# Revit family: BIMLIB_ДымовойСтеновойКлапан_SHSD_Прямоугольный_SHUFT
name_source: partatom
category: Арматура воздуховодов
revit_build: Autodesk Revit 2017 (Build: 20170118_1100(x64)
units: mm (PartAtom-declared; Revit-internal decimal feet)

## family parameters
Всегда вертикально = Да
На основе рабочей плоскости = Нет
Общий = Нет
При загрузке вырезать с полостями = Нет
Размер круглого соединителя = Использовать диаметр
Тип детали = Вставляется

## types (3) — shared parameters
ADSK_URL документации изделия = http://www.shuft.ru
ADSK_URL страницы изделия = http://www.shuft.ru
ADSK_Версия Revit = 2017
ADSK_Единица измерения = шт.
ADSK_Завод-изготовитель = ООО «Завод ВКО» марка SHUFT
ADSK_Классификация нагрузок = HVAC
ADSK_Материал = BIMLIB_Сталь_SHUFT
ADSK_Обозначение = ТУ 4854-032-21059055-2014
ADSK_Предел огнестойкости = EI120
BL_BIM library = https://bimlib.pro
BM_Климатическое исполнение = УХЛ4
L = 170 мм
URL = http://www.shuft.ru
Изготовитель = ООО «Завод ВКО» марка SHUFT
Описание = Предназначены для установки в стену, представляют собой прямоугольный корпус с минимальной длиной 180 мм с фланцем с одной стороны, внутри которого распологается привод
Плотность воздуха = 0.6100 кг/куб. м
Смещение центра = 20 мм

## per-type parameters (varying)
| type | Таблица |
| EI120, привод МВE | SHSD-120-MBE |
| EI120, привод R | SHSD-120-R |
| EI120, привод EM | SHSD-120-EM |
